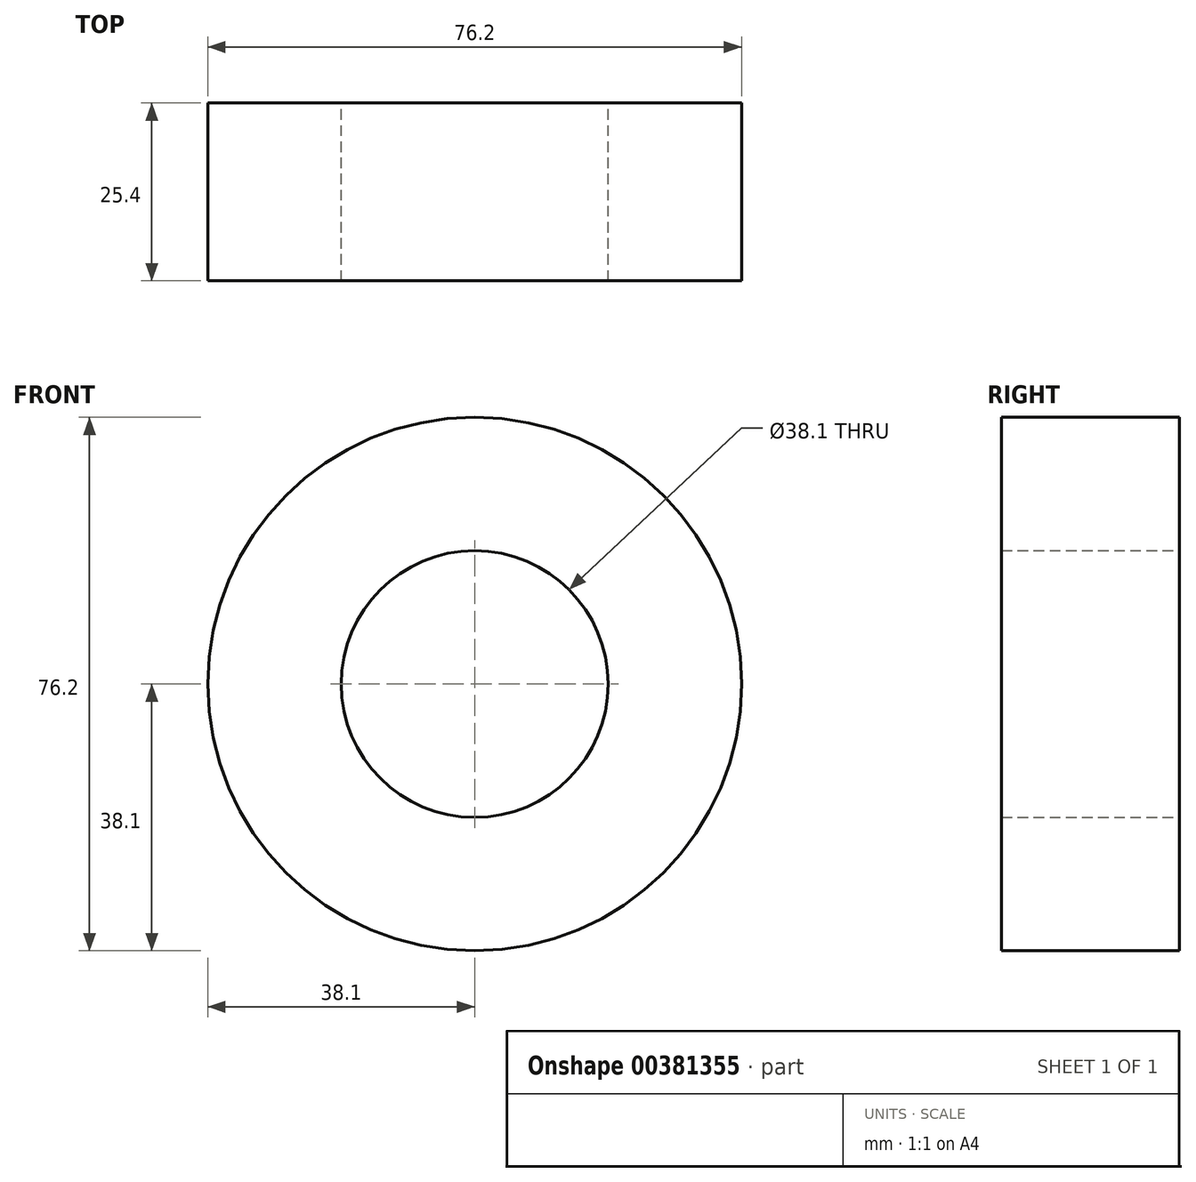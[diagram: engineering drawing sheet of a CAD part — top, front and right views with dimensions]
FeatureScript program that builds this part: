
annotation { "Feature Type Name" : "Feature", "Feature Type Description" : "" }
export const myFeature = defineFeature(function(context is Context, id is Id, definition is map)
    precondition{}
    {
        {
            var Q0;
            Q0=qCreatedBy(makeId("Front.planeOp"),FACE);
            var sketch = newSketch(context, id + "F0", { "sketchPlane" : qUnion([Q0])});
            skCircle(sketch, "E0", {"center": v(0, 0) * mm, "radius": 19.05 * mm});
            skCircle(sketch, "E1", {"center": v(0, 0) * mm, "radius": 38.1 * mm});
            skSolve(sketch);
        }
        {
            var Q0;
            Q0 = qSketchRegion(id + "F0", true);
            extrude(context, id + "F1", {"entities" : qUnion([Q0]), "depth" : 25.4 * mm});
        }
    });
